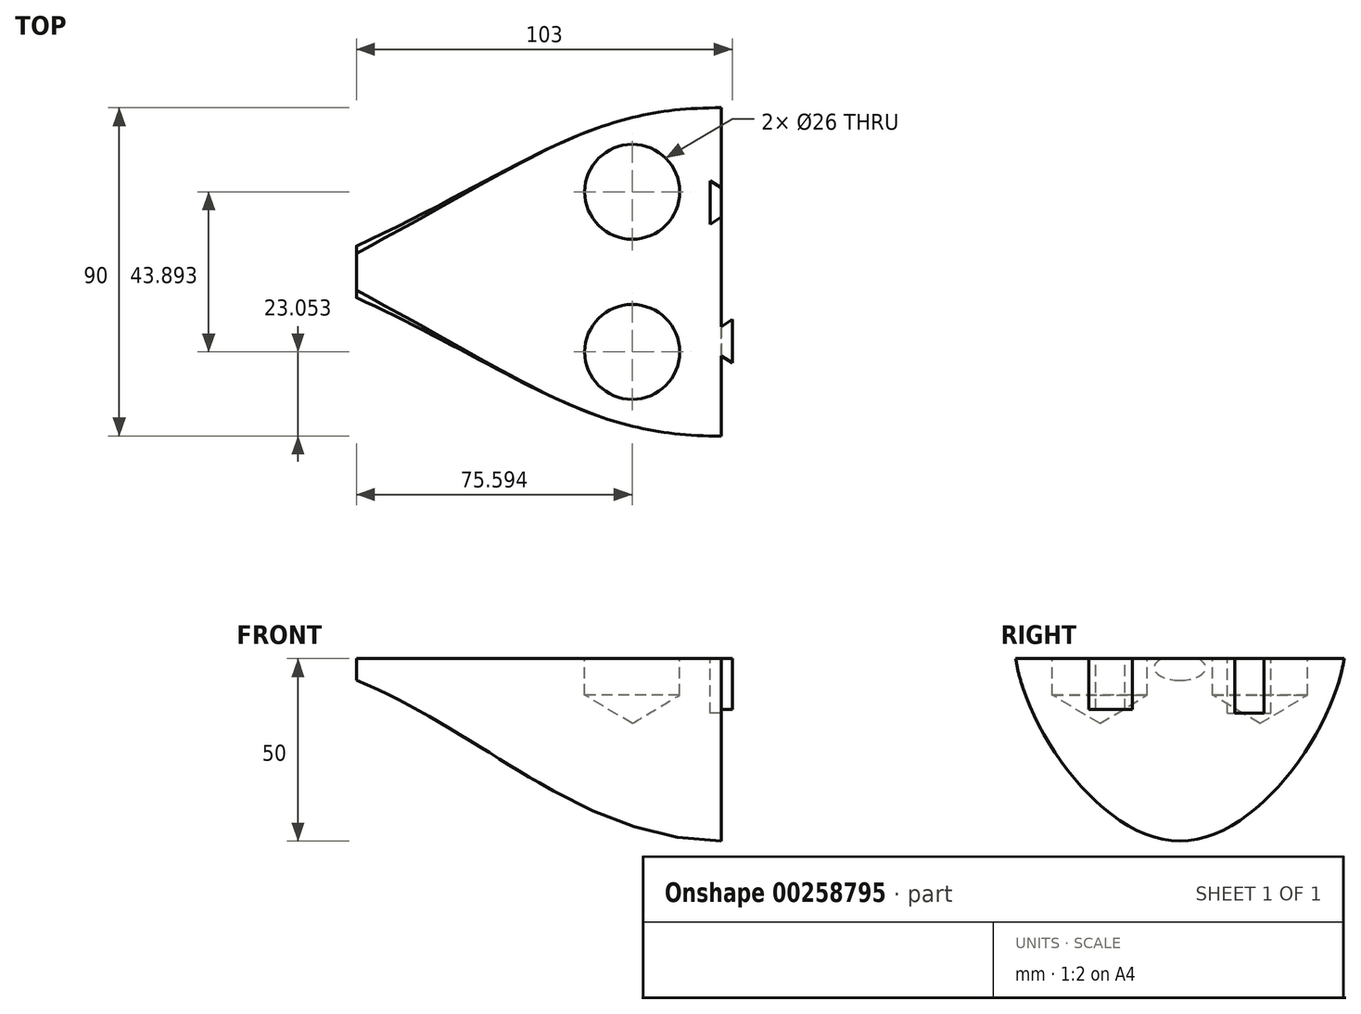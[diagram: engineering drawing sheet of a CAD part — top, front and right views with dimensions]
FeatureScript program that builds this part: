
annotation { "Feature Type Name" : "Feature", "Feature Type Description" : "" }
export const myFeature = defineFeature(function(context is Context, id is Id, definition is map)
    precondition{}
    {
        {
            var Q0;
            Q0=qCreatedBy(makeId("Right.planeOp"),FACE);
            var sketch = newSketch(context, id + "F0", { "sketchPlane" : qUnion([Q0])});
            skFitSpline(sketch, "E0", {"points": [v(-45, 0) * mm, v(0, -50) * mm, v(45, 0) * mm], "startDerivative": vector(18, -120) * mm, "endDerivative": vector(18, 120) * mm});
            skLineSegment(sketch, "E1", {"start": v(-45, 0) * mm, "end": v(0, 0) * mm});
            skLineSegment(sketch, "E2", {"start": v(0, 0) * mm, "end": v(45, 0) * mm});
            skSolve(sketch);
        }
        {
            var Q0;
            Q0=qCreatedBy(makeId("Right.planeOp"),FACE);
            cPlane(context, id + "F1", {"entities" : qUnion([Q0]), "cplaneType" : CPlaneType.OFFSET, "offset" : 100 * mm, "oppositeDirection" : true, "width" : 150 * mm, "height" : 150 * mm});
        }
        {
            var Q0;
            Q0=qCreatedBy(id+"F1.planeOp",FACE);
            var sketch = newSketch(context, id + "F2", { "sketchPlane" : qUnion([Q0])});
            skFitSpline(sketch, "E3", {"points": [v(-5, 0) * mm, v(0, -6) * mm, v(5, 0) * mm], "startDerivative": vector(-30, -18) * mm, "endDerivative": vector(-30, 18) * mm});
            skLineSegment(sketch, "E4", {"start": v(-5, 0) * mm, "end": v(0, 0) * mm});
            skLineSegment(sketch, "E5", {"start": v(0, 0) * mm, "end": v(5, 0) * mm});
            skSolve(sketch);
        }
        {
            var Q0;
            Q0=qCreatedBy(makeId("Top.planeOp"),FACE);
            var sketch = newSketch(context, id + "F3", { "sketchPlane" : qUnion([Q0])});
            skFitSpline(sketch, "E6", {"points": [v(-100, 5) * mm, v(0, 45) * mm], "startDerivative": vector(150, 81) * mm, "endDerivative": vector(105, 0) * mm});
            skSolve(sketch);
        }
        {
            var Q0;
            Q0=qCreatedBy(makeId("Top.planeOp"),FACE);
            var sketch = newSketch(context, id + "F4", { "sketchPlane" : qUnion([Q0])});
            skFitSpline(sketch, "E7", {"points": [v(-100, -5) * mm, v(0, -45) * mm], "startDerivative": vector(150, -81) * mm, "endDerivative": vector(105, 0) * mm});
            skSolve(sketch);
        }
        {
            var Q0;
            Q0=qCreatedBy(makeId("Front.planeOp"),FACE);
            var sketch = newSketch(context, id + "F5", { "sketchPlane" : qUnion([Q0])});
            skFitSpline(sketch, "E8", {"points": [v(-100, -6) * mm, v(0, -50) * mm], "startDerivative": vector(105, -42) * mm, "endDerivative": vector(115.32, 0) * mm});
            skSolve(sketch);
        }
        {
            var Q0;
            Q0=makeQuery(id+"F0.imprint","IMPRINT",FACE,{"disambiguationData":[TD([[makeQuery(id+"F0.imprint","IMPRINT",EDGE,{"derivedFrom":sQuery(id+"F0.wireOp",EDGE,"E0")}),1.0]])]});
            var Q1;
            Q1=makeQuery(id+"F2.imprint","IMPRINT",FACE,{"disambiguationData":[TD([[makeQuery(id+"F2.imprint","IMPRINT",EDGE,{"derivedFrom":sQuery(id+"F2.wireOp",EDGE,"E3")}),1.0]])]});
            var Q2;
            Q2=sQuery(id+"F4.wireOp",EDGE,"E7");
            var Q3;
            Q3=sQuery(id+"F5.wireOp",EDGE,"E8");
            var Q4;
            Q4=sQuery(id+"F3.wireOp",EDGE,"E6");
            loft(context, id + "F6", {"addGuides" : true, "sheetProfilesArray" : [{ "sheetProfileEntities" : qUnion([Q0]) }, { "sheetProfileEntities" : qUnion([Q1]) }], "guidesArray" : [{ "guideEntities" : qUnion([Q2]), "guideDerivativeType" : LoftGuideDerivativeType.DEFAULT, "guideDerivativeMagnitude" : 1 }, { "guideEntities" : qUnion([Q3]), "guideDerivativeType" : LoftGuideDerivativeType.DEFAULT, "guideDerivativeMagnitude" : 1 }, { "guideEntities" : qUnion([Q4]), "guideDerivativeType" : LoftGuideDerivativeType.DEFAULT, "guideDerivativeMagnitude" : 1 }]});
        }
        {
            var Q0;
            Q0=qCreatedBy(makeId("Top.planeOp"),FACE);
            var sketch = newSketch(context, id + "F7", { "sketchPlane" : qUnion([Q0])});
            skCircle(sketch, "E9", {"center": v(-24.4, 21.95) * mm, "radius": 13.37 * mm});
            skCircle(sketch, "E10.MirrorC", {"center": v(-24.4, -21.95) * mm, "radius": 13.37 * mm});
            skSolve(sketch);
        }
        {
            var Q0;
            Q0=sQuery(id+"F7.wireOp",VERTEX,"E9.center");
            var Q1;
            Q1=sQuery(id+"F7.wireOp",VERTEX,"E10.MirrorC.center");
            var Q2;
            Q2=makeQuery(id+"F6.opLoft","SWEPT_BODY",BODY,{"disambiguationData":[OSD([makeQuery(id+"F0.imprint","IMPRINT",FACE,{"disambiguationData":[TD([[makeQuery(id+"F0.imprint","IMPRINT",EDGE,{"derivedFrom":sQuery(id+"F0.wireOp",EDGE,"E0")}),1.0]])]}),makeQuery(id+"F2.imprint","IMPRINT",FACE,{"disambiguationData":[TD([[makeQuery(id+"F2.imprint","IMPRINT",EDGE,{"derivedFrom":sQuery(id+"F2.wireOp",EDGE,"E3")}),1.0]])]}),sQuery(id+"F3.wireOp",EDGE,"E6"),sQuery(id+"F4.wireOp",EDGE,"E7"),sQuery(id+"F5.wireOp",EDGE,"E8")])]});
            hole(context, id + "F8", {"style" : HoleStyle.SIMPLE, "endStyle" : HoleEndStyle.BLIND, "holeDiameter" : 26 * mm, "holeDepth" : 10 * mm, "tappedDepth" : 12 * mm, "tapClearance" : 3, "locations" : qUnion([Q0, Q1]), "scope" : qUnion([Q2])});
        }
        {
            var Q0;
            Q0=qCreatedBy(makeId("Top.planeOp"),FACE);
            var sketch = newSketch(context, id + "F9", { "sketchPlane" : qUnion([Q0])});
            skLineSegment(sketch, "E11", {"start": v(-8.67, 19) * mm, "end": v(10.73, 19) * mm, "construction": true});
            skLineSegment(sketch, "E12", {"start": v(-3, 13) * mm, "end": v(-3, 25) * mm});
            skLineSegment(sketch, "E13", {"start": v(-3, 25) * mm, "end": v(0, 23) * mm});
            skLineSegment(sketch, "E14", {"start": v(0, 23) * mm, "end": v(5, 23) * mm});
            skLineSegment(sketch, "E15", {"start": v(5, 23) * mm, "end": v(5, 15) * mm});
            skLineSegment(sketch, "E16", {"start": v(5, 15) * mm, "end": v(0, 15) * mm});
            skLineSegment(sketch, "E17", {"start": v(0, 15) * mm, "end": v(-3, 13) * mm});
            skSolve(sketch);
        }
        {
            var Q0;
            Q0=makeQuery(id+"F9.imprint","IMPRINT",FACE,{"disambiguationData":[TD([[makeQuery(id+"F9.imprint","IMPRINT",EDGE,{"derivedFrom":sQuery(id+"F9.wireOp",EDGE,"E12")}),-1.0]])]});
            extrude(context, id + "F10", {"entities" : qUnion([Q0]), "operationType" : NewBodyOperationType.REMOVE, "oppositeDirection" : true, "depth" : 15 * mm});
        }
        {
            var Q0;
            Q0=qCreatedBy(makeId("Top.planeOp"),FACE);
            var sketch = newSketch(context, id + "F11", { "sketchPlane" : qUnion([Q0])});
            skLineSegment(sketch, "E18", {"start": v(-6.28, -19) * mm, "end": v(8.64, -19) * mm, "construction": true});
            skLineSegment(sketch, "E19", {"start": v(-5, -15) * mm, "end": v(0, -15) * mm});
            skLineSegment(sketch, "E20", {"start": v(0, -15) * mm, "end": v(3, -13) * mm});
            skLineSegment(sketch, "E21", {"start": v(3, -13) * mm, "end": v(3, -25) * mm});
            skLineSegment(sketch, "E22", {"start": v(3, -25) * mm, "end": v(0, -23) * mm});
            skLineSegment(sketch, "E23", {"start": v(0, -23) * mm, "end": v(-5, -23) * mm});
            skLineSegment(sketch, "E24", {"start": v(-5, -23) * mm, "end": v(-5, -15) * mm});
            skSolve(sketch);
        }
        {
            var Q0;
            Q0=makeQuery(id+"F11.imprint","IMPRINT",FACE,{"disambiguationData":[TD([[makeQuery(id+"F11.imprint","IMPRINT",EDGE,{"derivedFrom":sQuery(id+"F11.wireOp",EDGE,"E19")}),-1.0]])]});
            extrude(context, id + "F12", {"entities" : qUnion([Q0]), "operationType" : NewBodyOperationType.ADD, "oppositeDirection" : true, "depth" : 14 * mm});
        }
    });
